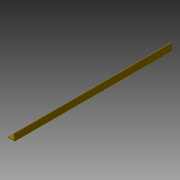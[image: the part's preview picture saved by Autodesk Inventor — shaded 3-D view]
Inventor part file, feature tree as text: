
AUTODESK INVENTOR PART (.ipt)
format: ipt  version: 2013 SP2 (Build 170200200, 200)  size: 72,192 bytes
history: native  units: mm
features: extrude x1, sketch x1
ambient origin geometry x8: Origin, YZ Plane, XZ Plane, XY Plane, X Axis, Y Axis, Z Axis, Center Point
bodies: Solid1 (feature_tree)
feature tree (2):
  extrude  "Extrusion1"  Depth=2.0mm
  sketch  "Sketch1"  dims[d0=20.0mm d1=2.0mm d2=2.0mm d3=20.0mm d4=455.0mm d5=0.0mm]
